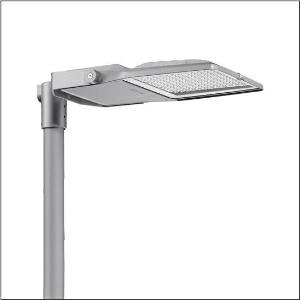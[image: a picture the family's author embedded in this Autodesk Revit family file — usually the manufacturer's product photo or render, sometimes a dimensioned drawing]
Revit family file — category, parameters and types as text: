
# Revit family: floodlight_fl_21_iq_midi___pl33t_5xa7781e2f3a_de32
name_source: partatom
category: Lighting Fixtures
units: mm (PartAtom-declared; Revit-internal decimal feet)

## family parameters
Cut with Voids When Loaded = No
Host = Face
Light Source = No
Part Type = Normal
Room Calculation Point = No
Round Connector Dimension = Use Diameter
Shared = No

## types (1)
- --- (1 x LED, 26540 lm, 208.1 W, 3000K)
    Apparent Load = 208 VA
    CIE Flux Codes = 26 75 99 100 100
    Color Rendering = 70
    Color Temperature = 3000K
    Default Elevation = 1800 mm
    Description = Floodlight FL 21 iQ midi, floodlight, primary light control with lens, of PMMA, primary optical cover: protective disc, of toughened safety glass, transparent, light distribution: PL33T, light emission: direct distribution, installation type: surface-mounted, LED, High Power LED, rated luminous flux: 26.540lm, luminous efficacy: 128lm/W, light colour: 730, colour temperature: 3000K, control gear: ECG iQ, control: optimised constant luminous flux control (CLO 2.0), Desk-Remote (wireless, voltage-free reading and setting of iQ features in the workshop via application-optimized NFC function/RFID function), Light-Fading, Smart-Wire, Night-Set, Lumen-Switch, Temp-Guard, Auto-Match, with terminal, 6-pole, mains connection: 220..240V, AC, 50/60Hz, start of lifetime: 208W, end of service life: 227W, reduction: 90W, luminaire housing, of diecast aluminium, powder-coated, Siteco® metallic grey (DB 702S), corrosivity category C5 mid according to DIN EN ISO 12944, sealing non-destructively replaceable, please order mast flange separately, mast bracket, of steel, galvanised, powder-coated, Siteco® metallic grey (DB 702S), protection rating (complete): IP66, insulation class (complete): insulation class II (safety insulation), certification: CE, protection symbol: D, impact resistance: IK08, permissible operating ambient temperature: -40..+40°C, permissible operating ambient temperature for outdoor applications: -40..+50°C, standard: DIN EN 12944, LABS conformity tested according to VDMA 24364:2018-05, packaging unit: 1 piece

Light Distribution: PL33T
    Height = 76 mm
    Lamp = 1 x LED
    Lamp Light Flux = 26540 lm
    Lamp Power = 208.1 W
    Lamp count = 1
    Length = 657 mm
    Luminous efficacy = 128 lm/W
    Manufacturer = Siteco
    ModVariant = No
    Model = 5XA7781E2F3A
    Number of Poles = 1
    OnlyDefault = Yes
    Power Factor = 1
    Product Name = Floodlight FL 21 iQ midi | PL33T
    Product group = floodlight | pylon annexe
    ProductGroupID = 6200
    Protection Class = Protection class II
    Protection Degree = IP 66
    RLX_Detail_Level = 1
    RLX_Emergency_Light_Flux = 0 lm
    RLX_Emergency_Type = 0
    RLX_Emergency_Type_DB = No
    RlxData = <blob elided: 154189 chars, md5=ce9da0a6>
    Socket = socket
    Standby Power = 0 W
    System Light Flux = 26540 lm
    System Power = 208 W
    Type Comments = factory setting: luminous flux: 100 % | dim-lin: 254 | 710 mA
    Type Image = l_1007123.jpg
    URL = http://relux.com
    VarID = @adj_034147
    Voltage = 0 V
    Weight = 0.00 kg
    Width = 442 mm

## geometry (parser evidence)
native form markers: Blend x4, Sweep x13
no freeform markers — native parametric forms only
